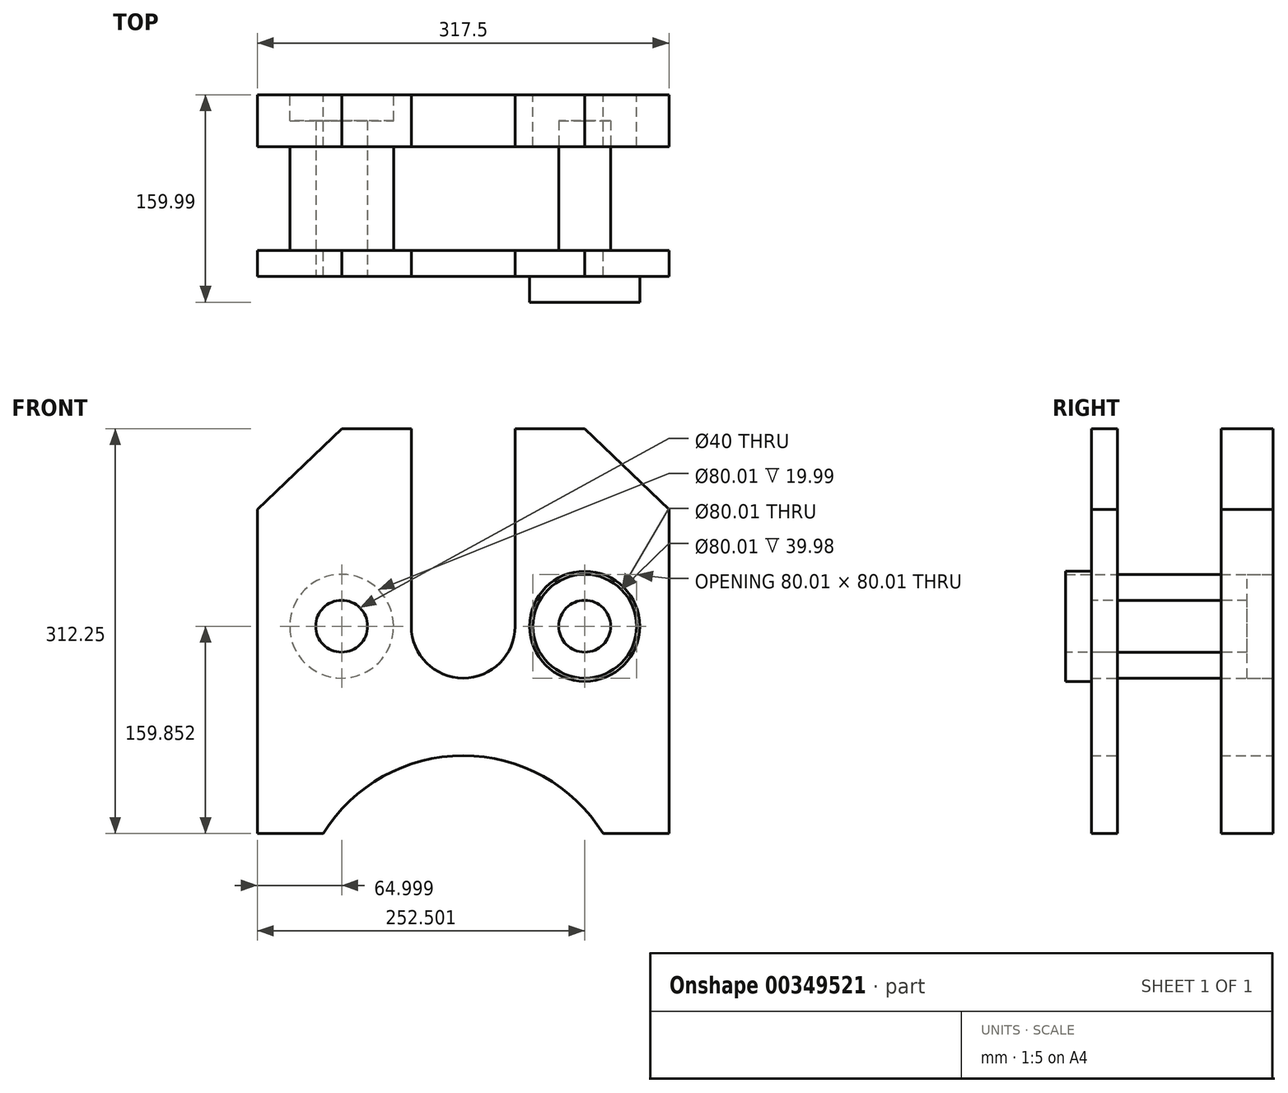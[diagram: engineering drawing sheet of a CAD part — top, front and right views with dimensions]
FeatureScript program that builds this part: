
annotation { "Feature Type Name" : "Feature", "Feature Type Description" : "" }
export const myFeature = defineFeature(function(context is Context, id is Id, definition is map)
    precondition{}
    {
        {
            var Q0;
            Q0=qCreatedBy(makeId("Front.planeOp"),FACE);
            var sketch = newSketch(context, id + "F0", { "sketchPlane" : qUnion([Q0])});
            skArc(sketch, "E0", {"start": v(107.95, 0) * mm, "mid": v(0, 60.1) * mm, "end": v(-107.95, 0) * mm});
            skLineSegment(sketch, "E1", {"start": v(107.95, 0) * mm, "end": v(158.75, 0) * mm});
            skLineSegment(sketch, "E2", {"start": v(158.75, 0) * mm, "end": v(158.75, 250.01) * mm});
            skLineSegment(sketch, "E3", {"start": v(158.75, 250.01) * mm, "end": v(93.75, 312.25) * mm});
            skLineSegment(sketch, "E4", {"start": v(93.75, 312.25) * mm, "end": v(40, 312.25) * mm});
            skLineSegment(sketch, "E5", {"start": v(40, 312.25) * mm, "end": v(40, 159.85) * mm});
            skCircle(sketch, "E6", {"center": v(93.75, 159.85) * mm, "radius": 40 * mm});
            skLineSegment(sketch, "E7.MirrorCS", {"start": v(-107.95, 0) * mm, "end": v(-158.75, 0) * mm});
            skCircle(sketch, "E8.MirrorC", {"center": v(-93.75, 159.85) * mm, "radius": 40 * mm});
            skLineSegment(sketch, "E9.MirrorCS", {"start": v(-158.75, 0) * mm, "end": v(-158.75, 250.01) * mm});
            skLineSegment(sketch, "E10.MirrorCS", {"start": v(-40, 312.25) * mm, "end": v(-40, 159.85) * mm});
            skLineSegment(sketch, "E11.MirrorCS", {"start": v(-158.75, 250.01) * mm, "end": v(-93.75, 312.25) * mm});
            skLineSegment(sketch, "E12.MirrorCS", {"start": v(-93.75, 312.25) * mm, "end": v(-40, 312.25) * mm});
            skArc(sketch, "E13", {"start": v(-40, 159.85) * mm, "mid": v(0, 119.85) * mm, "end": v(40, 159.85) * mm});
            skSolve(sketch);
        }
        {
            var Q0;
            Q0=makeQuery(id+"F0.imprint","IMPRINT",FACE,{"disambiguationData":[TD([[makeQuery(id+"F0.imprint","IMPRINT",EDGE,{"derivedFrom":sQuery(id+"F0.wireOp",EDGE,"E0")}),-1.0]])]});
            extrude(context, id + "F1", {"entities" : qUnion([Q0]), "depth" : 160 * mm});
        }
        {
            var Q0;
            Q0=makeQuery(id+"F1.opExtrude","SWEPT_FACE",FACE,{"disambiguationData":[OSD([sQuery(id+"F0.wireOp",EDGE,"E2")])]});
            var sketch = newSketch(context, id + "F2", { "sketchPlane" : qUnion([Q0])});
            skLineSegment(sketch, "E14.bottom", {"start": v(-120.02, 0) * mm, "end": v(-40, 0) * mm});
            skLineSegment(sketch, "E14.top", {"start": v(-120.02, 312.42) * mm, "end": v(-40, 312.42) * mm});
            skLineSegment(sketch, "E14.left", {"start": v(-120.02, 0) * mm, "end": v(-120.02, 312.42) * mm});
            skLineSegment(sketch, "E14.right", {"start": v(-40, 0) * mm, "end": v(-40, 312.42) * mm});
            skSolve(sketch);
        }
        {
            var Q0;
            {var subQ0=sQuery(id+"F2.wireOp",EDGE,"E14.top");Q0=makeQuery(id+"F2.imprint","IMPRINT",FACE,{"disambiguationData":[TD([[makeQuery(id+"F2.imprint","IMPRINT",EDGE,{"derivedFrom":subQ0}),-1.0]])]});}
            var Q1;
            {var subQ0=sQuery(id+"F2.wireOp",EDGE,"E14.bottom");Q1=makeQuery(id+"F2.imprint","IMPRINT",FACE,{"disambiguationData":[TD([[makeQuery(id+"F2.imprint","IMPRINT",EDGE,{"derivedFrom":subQ0}),1.0]])]});}
            extrude(context, id + "F3", {"entities" : qUnion([Q0, Q1]), "operationType" : NewBodyOperationType.REMOVE, "oppositeDirection" : true, "depth" : 398.78 * mm});
        }
        {
            var Q0;
            Q0=makeQuery(id+"F1.opExtrude","CAP_FACE",FACE,{"disambiguationData":[OSD([sQuery(id+"F0.wireOp",EDGE,"E0"),sQuery(id+"F0.wireOp",EDGE,"E1"),sQuery(id+"F0.wireOp",EDGE,"E2"),sQuery(id+"F0.wireOp",EDGE,"E3"),sQuery(id+"F0.wireOp",EDGE,"E4"),sQuery(id+"F0.wireOp",EDGE,"E5"),sQuery(id+"F0.wireOp",EDGE,"E6"),sQuery(id+"F0.wireOp",EDGE,"E7.MirrorCS"),sQuery(id+"F0.wireOp",EDGE,"E8.MirrorC"),sQuery(id+"F0.wireOp",EDGE,"E9.MirrorCS"),sQuery(id+"F0.wireOp",EDGE,"E10.MirrorCS"),sQuery(id+"F0.wireOp",EDGE,"E11.MirrorCS"),sQuery(id+"F0.wireOp",EDGE,"E12.MirrorCS"),sQuery(id+"F0.wireOp",EDGE,"E13")])],"isStart":false});
            var sketch = newSketch(context, id + "F4", { "sketchPlane" : qUnion([Q0])});
            skCircle(sketch, "E15", {"center": v(-93.75, 159.85) * mm, "radius": 20 * mm});
            skCircle(sketch, "E16", {"center": v(-93.75, 159.85) * mm, "radius": 42.5 * mm});
            skCircle(sketch, "E17.MirrorC", {"center": v(93.75, 159.85) * mm, "radius": 42.5 * mm});
            skCircle(sketch, "E18.MirrorC", {"center": v(93.75, 159.85) * mm, "radius": 20 * mm});
            skSolve(sketch);
        }
        {
            var Q0;
            Q0=makeQuery(id+"F4.imprint","IMPRINT",FACE,{"disambiguationData":[TD([[makeQuery(id+"F4.imprint","IMPRINT",EDGE,{"derivedFrom":sQuery(id+"F4.wireOp",EDGE,"E15")}),-1.0]])]});
            var Q1;
            Q1=makeQuery(id+"F4.imprint","IMPRINT",FACE,{"disambiguationData":[TD([[makeQuery(id+"F4.imprint","IMPRINT",EDGE,{"derivedFrom":sQuery(id+"F4.wireOp",EDGE,"E18.MirrorC")}),1.0]])]});
            extrude(context, id + "F5", {"entities" : qUnion([Q0, Q1]), "operationType" : NewBodyOperationType.ADD, "oppositeDirection" : true, "depth" : 140 * mm});
        }
        {
            var Q0;
            {var subQ0=sQuery(id+"F0.wireOp",EDGE,"E6");var subQ1=sQuery(id+"F0.wireOp",EDGE,"E8.MirrorC");Q0=makeQuery(id+"F5.boolean.opBoolean","MERGE",FACE,{"derivedFrom":[makeQuery(id+"F1.opExtrude","CAP_FACE",FACE,{"disambiguationData":[OSD([sQuery(id+"F0.wireOp",EDGE,"E0"),sQuery(id+"F0.wireOp",EDGE,"E1"),sQuery(id+"F0.wireOp",EDGE,"E2"),sQuery(id+"F0.wireOp",EDGE,"E3"),sQuery(id+"F0.wireOp",EDGE,"E4"),sQuery(id+"F0.wireOp",EDGE,"E5"),subQ0,sQuery(id+"F0.wireOp",EDGE,"E7.MirrorCS"),subQ1,sQuery(id+"F0.wireOp",EDGE,"E9.MirrorCS"),sQuery(id+"F0.wireOp",EDGE,"E10.MirrorCS"),sQuery(id+"F0.wireOp",EDGE,"E11.MirrorCS"),sQuery(id+"F0.wireOp",EDGE,"E12.MirrorCS"),sQuery(id+"F0.wireOp",EDGE,"E13")])],"isStart":false}),makeQuery(id+"F5.opExtrude","CAP_FACE",FACE,{"disambiguationData":[OSD([subQ1,sQuery(id+"F4.wireOp",EDGE,"E15")])],"isStart":true}),makeQuery(id+"F5.opExtrude","CAP_FACE",FACE,{"disambiguationData":[OSD([subQ0,sQuery(id+"F4.wireOp",EDGE,"E18.MirrorC")])],"isStart":true})]});}
            var sketch = newSketch(context, id + "F6", { "sketchPlane" : qUnion([Q0])});
            skCircle(sketch, "E19", {"center": v(-93.75, 159.85) * mm, "radius": 42.5 * mm});
            skCircle(sketch, "E20.MirrorC", {"center": v(93.75, 159.85) * mm, "radius": 42.5 * mm});
            skSolve(sketch);
        }
        {
            var Q0;
            Q0=makeQuery(id+"F6.imprint","IMPRINT",FACE,{"disambiguationData":[TD([[makeQuery(id+"F6.imprint","IMPRINT",EDGE,{"derivedFrom":sQuery(id+"F6.wireOp",EDGE,"E19")}),1.0]])]});
            var Q1;
            Q1=makeQuery(id+"F6.imprint","IMPRINT",FACE,{"disambiguationData":[TD([[makeQuery(id+"F6.imprint","IMPRINT",EDGE,{"derivedFrom":sQuery(id+"F6.wireOp",EDGE,"E20.MirrorC")}),-1.0]])]});
            extrude(context, id + "F7", {"entities" : qUnion([Q0, Q1]), "operationType" : NewBodyOperationType.REMOVE, "oppositeDirection" : true, "depth" : 19.99 * mm});
        }
    });
